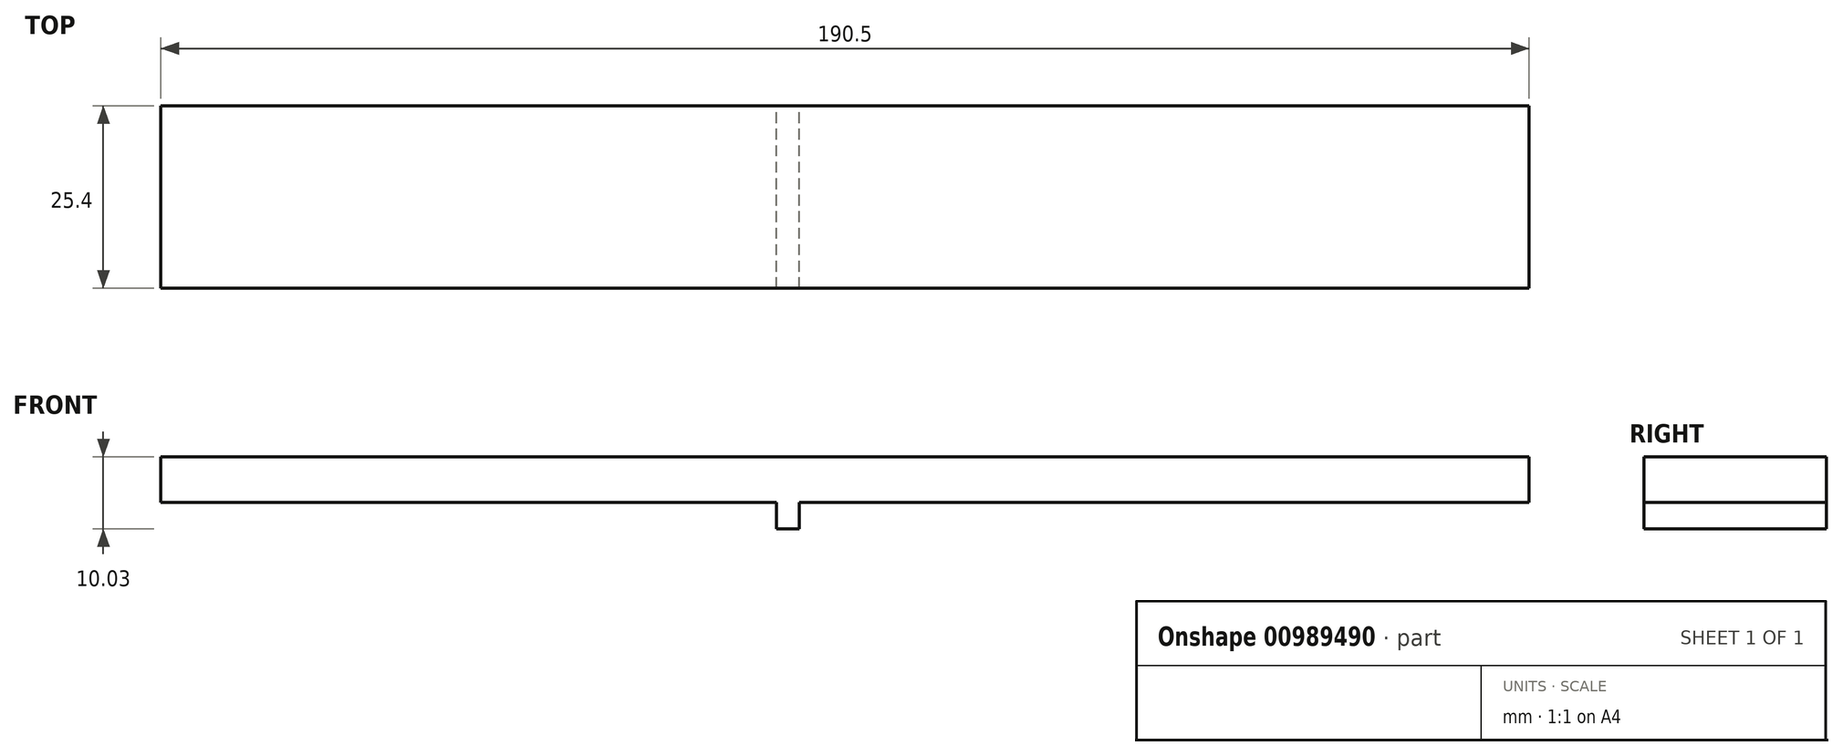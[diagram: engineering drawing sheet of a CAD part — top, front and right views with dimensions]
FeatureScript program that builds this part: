
annotation { "Feature Type Name" : "Feature", "Feature Type Description" : "" }
export const myFeature = defineFeature(function(context is Context, id is Id, definition is map)
    precondition{}
    {
        {
            var Q0;
            Q0=qCreatedBy(makeId("Front.planeOp"),FACE);
            var sketch = newSketch(context, id + "F0", { "sketchPlane" : qUnion([Q0])});
            skLineSegment(sketch, "E0", {"start": v(-106.24, 15.38) * mm, "end": v(84.26, 15.38) * mm});
            skLineSegment(sketch, "E1", {"start": v(84.26, 15.38) * mm, "end": v(84.26, 9.03) * mm});
            skLineSegment(sketch, "E2", {"start": v(84.26, 9.03) * mm, "end": v(-17.34, 9.03) * mm});
            skLineSegment(sketch, "E3", {"start": v(-17.34, 9.03) * mm, "end": v(-17.34, 5.35) * mm});
            skLineSegment(sketch, "E4", {"start": v(-17.34, 5.35) * mm, "end": v(-20.51, 5.35) * mm});
            skLineSegment(sketch, "E5", {"start": v(-106.24, 15.38) * mm, "end": v(-106.24, 9.03) * mm});
            skLineSegment(sketch, "E6", {"start": v(-106.24, 9.03) * mm, "end": v(-20.51, 9.03) * mm});
            skLineSegment(sketch, "E7", {"start": v(-20.51, 9.03) * mm, "end": v(-20.51, 5.35) * mm});
            skSolve(sketch);
        }
        {
            var Q0;
            Q0=makeQuery(id+"F0.imprint","IMPRINT",FACE,{"disambiguationData":[TD([[makeQuery(id+"F0.imprint","IMPRINT",EDGE,{"derivedFrom":sQuery(id+"F0.wireOp",EDGE,"E0")}),-1.0]])]});
            extrude(context, id + "F1", {"entities" : qUnion([Q0]), "depth" : 25.4 * mm, "offsetDistance" : 25.4 * mm});
        }
    });
